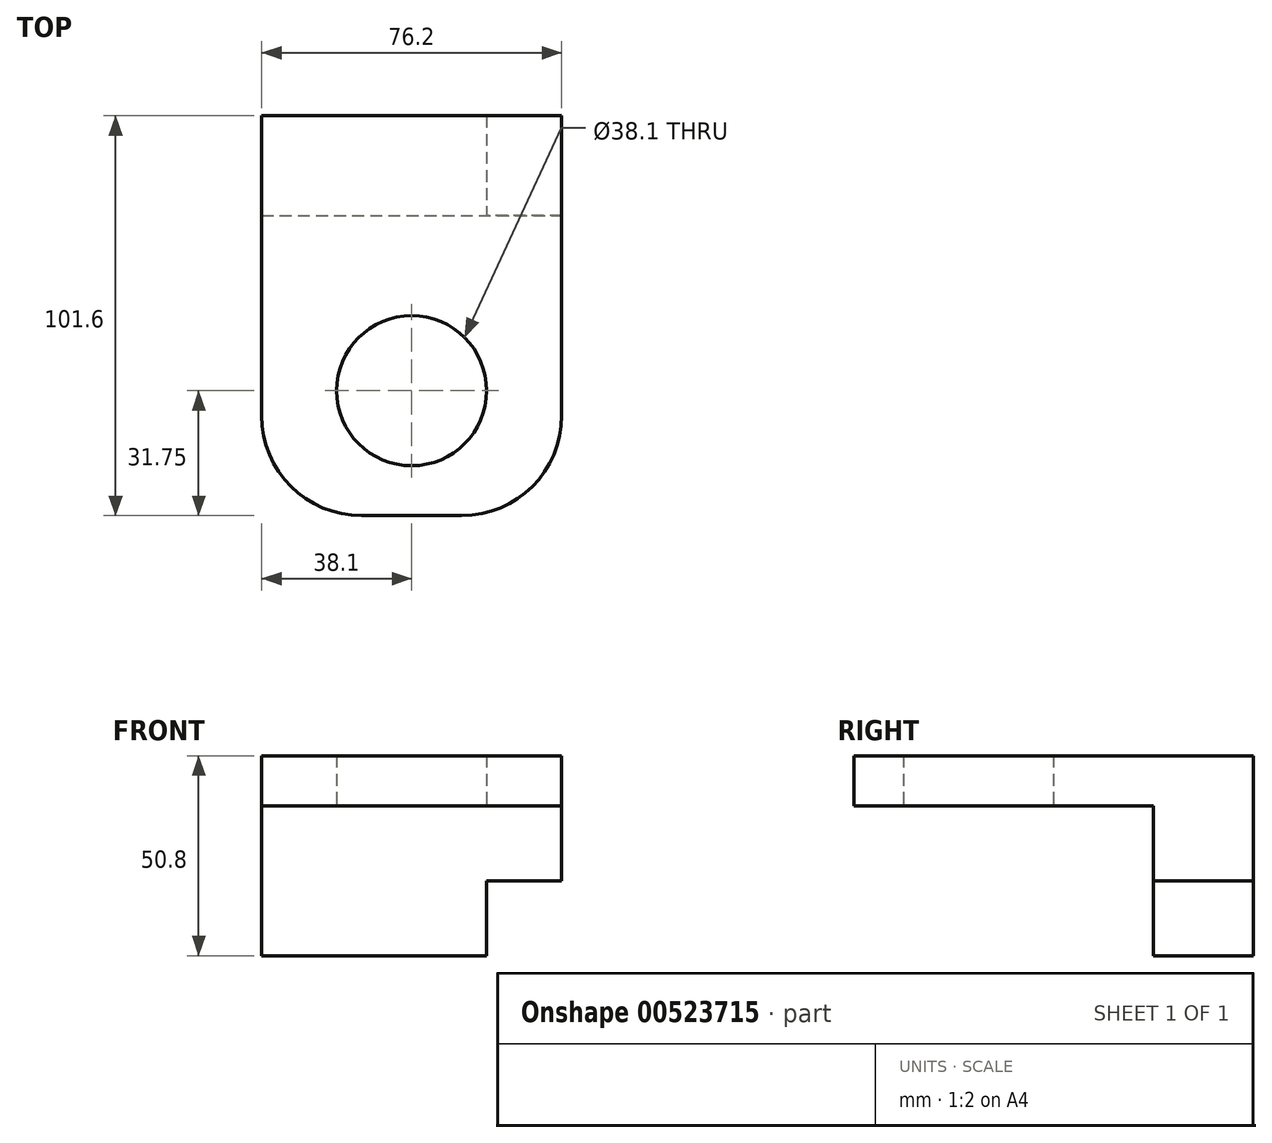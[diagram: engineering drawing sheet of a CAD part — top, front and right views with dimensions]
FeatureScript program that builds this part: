
annotation { "Feature Type Name" : "Feature", "Feature Type Description" : "" }
export const myFeature = defineFeature(function(context is Context, id is Id, definition is map)
    precondition{}
    {
        {
            var Q0;
            Q0=qCreatedBy(makeId("Top.planeOp"),FACE);
            var sketch = newSketch(context, id + "F0", { "sketchPlane" : qUnion([Q0])});
            skLineSegment(sketch, "E0.bottom", {"start": v(38.1, 50.8) * mm, "end": v(-38.1, 50.8) * mm});
            skLineSegment(sketch, "E0.top", {"start": v(38.1, -50.8) * mm, "end": v(-38.1, -50.8) * mm});
            skLineSegment(sketch, "E0.left", {"start": v(38.1, 50.8) * mm, "end": v(38.1, -50.8) * mm});
            skLineSegment(sketch, "E0.right", {"start": v(-38.1, 50.8) * mm, "end": v(-38.1, -50.8) * mm});
            skPoint(sketch, "E0.middle", {"position": v(0, 0) * mm});
            skSolve(sketch);
        }
        {
            var Q0;
            Q0=makeQuery(id+"F0.imprint","IMPRINT",FACE,{"disambiguationData":[TD([[makeQuery(id+"F0.imprint","IMPRINT",EDGE,{"derivedFrom":sQuery(id+"F0.wireOp",EDGE,"E0.bottom")}),1.0]])]});
            extrude(context, id + "F1", {"entities" : qUnion([Q0]), "depth" : 12.7 * mm, "offsetDistance" : 25.4 * mm});
        }
        {
            var Q0;
            Q0=qCreatedBy(makeId("Top.planeOp"),FACE);
            var sketch = newSketch(context, id + "F2", { "sketchPlane" : qUnion([Q0])});
            skCircle(sketch, "E1", {"center": v(0, -19.05) * mm, "radius": 19.05 * mm});
            skSolve(sketch);
        }
        {
            var Q0;
            Q0=makeQuery(id+"F2.imprint","IMPRINT",FACE,{"disambiguationData":[TD([[makeQuery(id+"F2.imprint","IMPRINT",EDGE,{"derivedFrom":sQuery(id+"F2.wireOp",EDGE,"E1")}),1.0]])]});
            extrude(context, id + "F3", {"entities" : qUnion([Q0]), "operationType" : NewBodyOperationType.REMOVE, "depth" : 25.4 * mm, "offsetDistance" : 25.4 * mm});
        }
        {
            var Q0;
            Q0=qCreatedBy(makeId("Top.planeOp"),FACE);
            var sketch = newSketch(context, id + "F4", { "sketchPlane" : qUnion([Q0])});
            skLineSegment(sketch, "E2.bottom", {"start": v(-38.1, 50.8) * mm, "end": v(38.1, 50.8) * mm});
            skLineSegment(sketch, "E2.top", {"start": v(-38.1, 25.4) * mm, "end": v(38.1, 25.4) * mm});
            skLineSegment(sketch, "E2.left", {"start": v(-38.1, 50.8) * mm, "end": v(-38.1, 25.4) * mm});
            skLineSegment(sketch, "E2.right", {"start": v(38.1, 50.8) * mm, "end": v(38.1, 25.4) * mm});
            skSolve(sketch);
        }
        {
            var Q0;
            Q0=makeQuery(id+"F4.imprint","IMPRINT",FACE,{"disambiguationData":[TD([[makeQuery(id+"F4.imprint","IMPRINT",EDGE,{"derivedFrom":sQuery(id+"F4.wireOp",EDGE,"E2.bottom")}),-1.0]])]});
            extrude(context, id + "F5", {"entities" : qUnion([Q0]), "operationType" : NewBodyOperationType.ADD, "oppositeDirection" : true, "depth" : 38.1 * mm, "offsetDistance" : 25.4 * mm});
        }
        {
            var Q0;
            Q0=makeQuery(id+"F5.opExtrude","SWEPT_FACE",FACE,{"disambiguationData":[OSD([sQuery(id+"F4.wireOp",EDGE,"E2.top")])]});
            var sketch = newSketch(context, id + "F6", { "sketchPlane" : qUnion([Q0])});
            skLineSegment(sketch, "E3.bottom", {"start": v(38.1, -38.1) * mm, "end": v(19.05, -38.1) * mm});
            skLineSegment(sketch, "E3.top", {"start": v(38.1, -19.05) * mm, "end": v(19.05, -19.05) * mm});
            skLineSegment(sketch, "E3.left", {"start": v(38.1, -38.1) * mm, "end": v(38.1, -19.05) * mm});
            skLineSegment(sketch, "E3.right", {"start": v(19.05, -38.1) * mm, "end": v(19.05, -19.05) * mm});
            skSolve(sketch);
        }
        {
            var Q0;
            Q0=makeQuery(id+"F6.imprint","IMPRINT",FACE,{"disambiguationData":[TD([[makeQuery(id+"F6.imprint","IMPRINT",EDGE,{"derivedFrom":sQuery(id+"F6.wireOp",EDGE,"E3.bottom")}),1.0]])]});
            extrude(context, id + "F7", {"entities" : qUnion([Q0]), "operationType" : NewBodyOperationType.REMOVE, "oppositeDirection" : true, "depth" : 25.4 * mm, "offsetDistance" : 25.4 * mm});
        }
        {
            var Q0;
            Q0=makeQuery(id+"F1.opExtrude","SWEPT_EDGE",EDGE,{"disambiguationData":[OSD([sQuery(id+"F0.wireOp",EDGE,"E0.top"),sQuery(id+"F0.wireOp",EDGE,"E0.left")])]});
            var Q1;
            Q1=makeQuery(id+"F1.opExtrude","SWEPT_EDGE",EDGE,{"disambiguationData":[OSD([sQuery(id+"F0.wireOp",EDGE,"E0.top"),sQuery(id+"F0.wireOp",EDGE,"E0.right")])]});
            fillet(context, id + "F8", {"entities" : qUnion([Q0, Q1]), "radius" : 25.4 * mm, "tangentPropagation" : true, "allowEdgeOverflow" : false});
        }
    });
